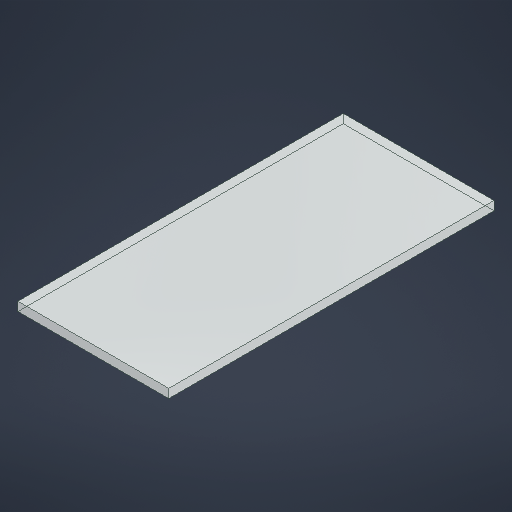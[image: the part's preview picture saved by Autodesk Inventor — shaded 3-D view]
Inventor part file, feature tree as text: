
AUTODESK INVENTOR PART (.ipt)
format: ipt  version: 2025 (Build 290162000, 162)  size: 198,656 bytes
history: native  units: in
note: dims shown in document units (in); Inventor stores cm internally (conversion verified against a paired STEP export)
features: extrude x1, sketch x1
ambient origin geometry x8: Origin, YZ Plane, XZ Plane, XY Plane, X Axis, Y Axis, Z Axis, Center Point
bodies: Solid1 (feature_tree)
feature tree (2):
  extrude  "Extrusion1"  Depth=4.3307in
  sketch  "Sketch1"  dims[d0=2.0079in d1=4.3307in d2=0.1181in d3=0.0in]
